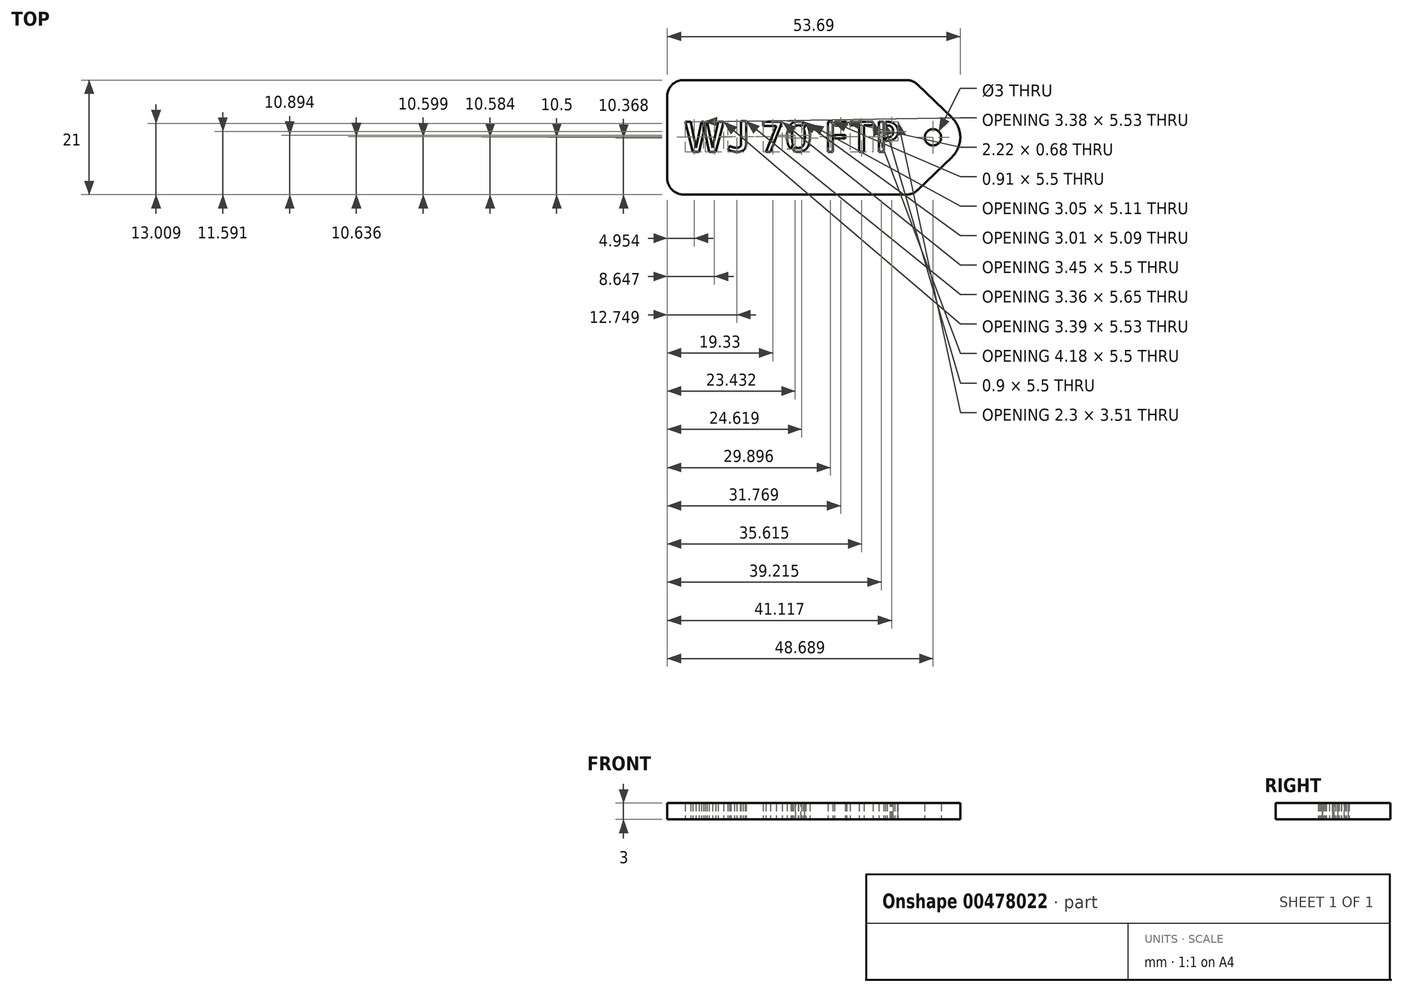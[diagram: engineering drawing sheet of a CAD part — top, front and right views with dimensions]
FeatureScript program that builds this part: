
annotation { "Feature Type Name" : "Feature", "Feature Type Description" : "" }
export const myFeature = defineFeature(function(context is Context, id is Id, definition is map)
    precondition{}
    {
        {
            var Q0;
            Q0=qCreatedBy(makeId("Top.planeOp"),FACE);
            var sketch = newSketch(context, id + "F0", { "sketchPlane" : qUnion([Q0])});
            skLineSegment(sketch, "E0.bottom", {"start": v(22.5, 10.5) * mm, "end": v(-19.5, 10.5) * mm});
            skLineSegment(sketch, "E0.top", {"start": v(22.5, -10.5) * mm, "end": v(-19.5, -10.5) * mm});
            skLineSegment(sketch, "E0.right", {"start": v(-22.5, 7.5) * mm, "end": v(-22.5, -7.5) * mm});
            skPoint(sketch, "E0.middle", {"position": v(0, 0) * mm});
            skPoint(sketch, "E1.visualSharp", {"position": v(-22.5, 10.5) * mm});
            skArc(sketch, "E1.filletArc", {"start": v(-19.5, 10.5) * mm, "mid": v(-21.62, 9.62) * mm, "end": v(-22.5, 7.5) * mm});
            skPoint(sketch, "E2.visualSharp", {"position": v(-22.5, -10.5) * mm});
            skArc(sketch, "E2.filletArc", {"start": v(-22.5, -7.5) * mm, "mid": v(-21.62, -9.62) * mm, "end": v(-19.5, -10.5) * mm});
            skLineSegment(sketch, "E3", {"start": v(22.5, 10.5) * mm, "end": v(29.66, 3.6) * mm});
            skLineSegment(sketch, "E4", {"start": v(29.66, -3.6) * mm, "end": v(22.5, -10.5) * mm});
            skPoint(sketch, "E5.visualSharp", {"position": v(33.4, 0) * mm});
            skArc(sketch, "E5.filletArc", {"start": v(29.66, -3.6) * mm, "mid": v(31.19, 0) * mm, "end": v(29.66, 3.6) * mm});
            skCircle(sketch, "E6", {"center": v(26.19, 0) * mm, "radius": 1.5 * mm});
            skSolve(sketch);
        }
        {
            var Q0;
            Q0=makeQuery(id+"F0.imprint","IMPRINT",FACE,{"disambiguationData":[TD([[makeQuery(id+"F0.imprint","IMPRINT",EDGE,{"derivedFrom":sQuery(id+"F0.wireOp",EDGE,"E0.bottom")}),1.0]])]});
            extrude(context, id + "F1", {"entities" : qUnion([Q0]), "flatOperationType" : FlatOperationType.REMOVE, "offsetDistance" : 25 * mm, "depth" : 3 * mm, "domain" : OperationDomain.MODEL});
        }
        {
            var Q0;
            Q0=qCreatedBy(makeId("Top.planeOp"),FACE);
            var sketch = newSketch(context, id + "F2", { "sketchPlane" : qUnion([Q0])});
            skText(sketch, "E7", { "text": "WJ 70 FTP", "fontName": "AllertaStencil-Regular.ttf"});
            const initialGuessF2  = {"E7": [-0.01978, -0.00265, 1, 0, 0.0055]};
            skSetInitialGuess(sketch, initialGuessF2);
            skSolve(sketch);
        }
        {
            var Q0;
            Q0 = qSketchRegion(id + "F2", true);
            extrude(context, id + "F3", {"entities" : qUnion([Q0]), "operationType" : NewBodyOperationType.REMOVE, "endBound" : BoundingType.THROUGH_ALL, "depth" : 25 * mm});
        }
        {
            var Q0;
            Q0=makeQuery(id+"F1.opExtrude","SWEPT_EDGE",EDGE,{"disambiguationData":[OSD([sQuery(id+"F0.wireOp",EDGE,"E0.bottom"),sQuery(id+"F0.wireOp",EDGE,"E3")])]});
            var Q1;
            Q1=makeQuery(id+"F1.opExtrude","SWEPT_EDGE",EDGE,{"disambiguationData":[OSD([sQuery(id+"F0.wireOp",EDGE,"E0.top"),sQuery(id+"F0.wireOp",EDGE,"E4")])]});
            fillet(context, id + "F4", {"entities" : qUnion([Q0, Q1]), "radius" : 3 * mm, "tangentPropagation" : true, "allowEdgeOverflow" : false});
        }
    });
